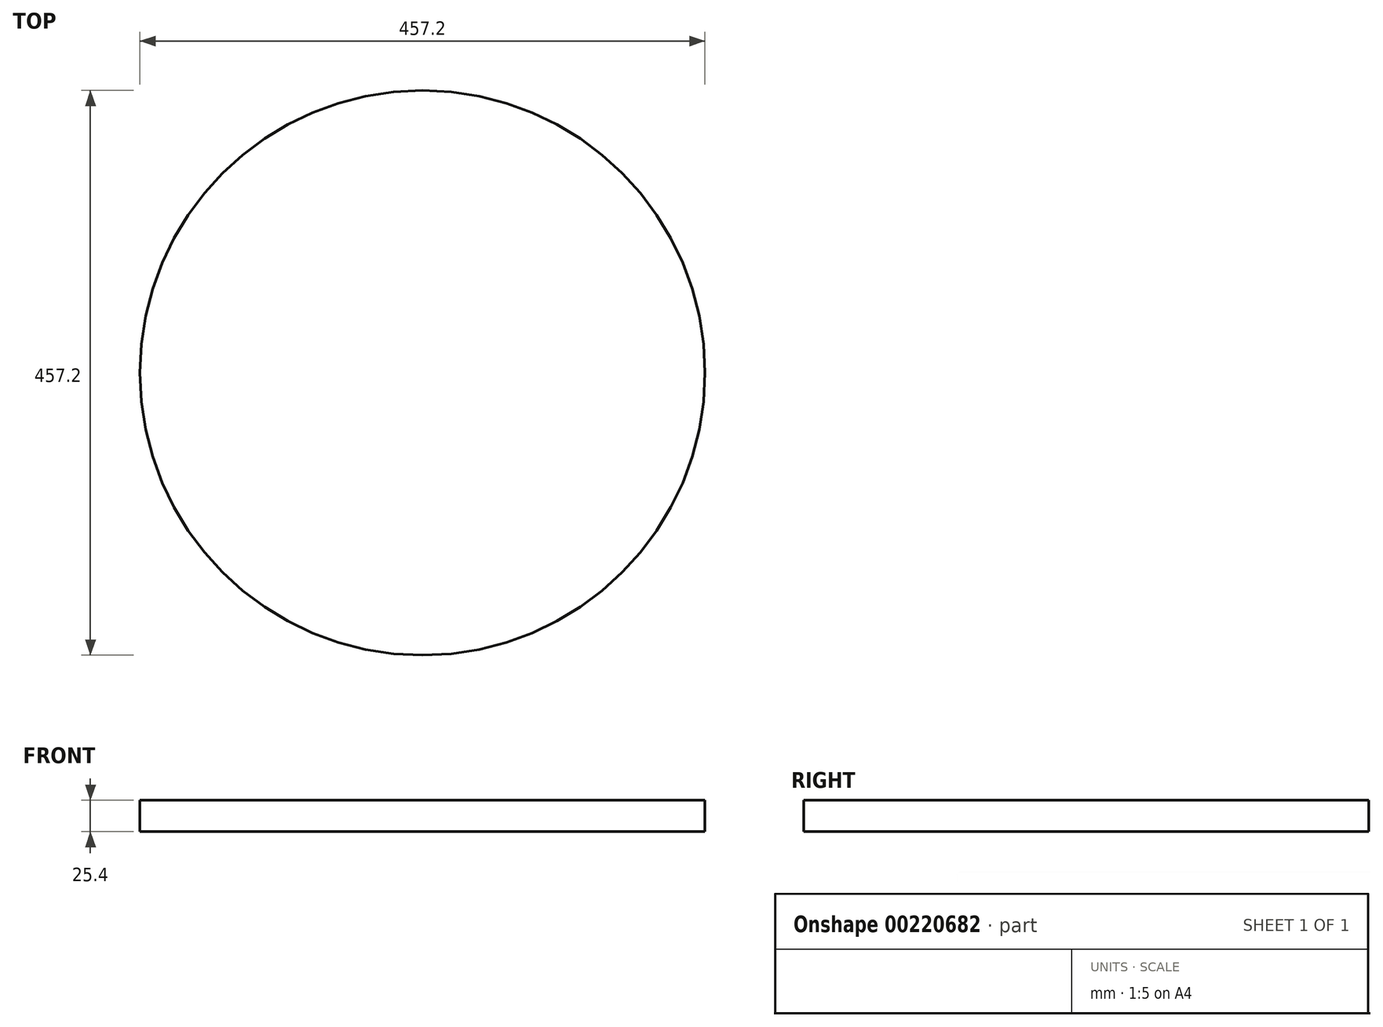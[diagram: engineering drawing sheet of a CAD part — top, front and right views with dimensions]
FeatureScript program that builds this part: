
annotation { "Feature Type Name" : "Feature", "Feature Type Description" : "" }
export const myFeature = defineFeature(function(context is Context, id is Id, definition is map)
    precondition{}
    {
        {
            var Q0;
            Q0=qCreatedBy(makeId("Top.planeOp"),FACE);
            var sketch = newSketch(context, id + "F0", { "sketchPlane" : qUnion([Q0])});
            skCircle(sketch, "E0", {"center": v(0, 0) * mm, "radius": 228.6 * mm});
            skSolve(sketch);
        }
        {
            var Q0;
            Q0 = qSketchRegion(id + "F0", true);
            extrude(context, id + "F1", {"entities" : qUnion([Q0]), "depth" : 25.4 * mm});
        }
    });
